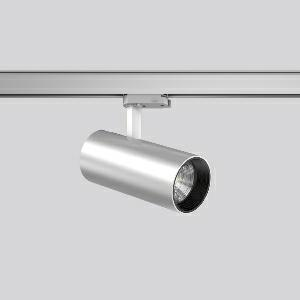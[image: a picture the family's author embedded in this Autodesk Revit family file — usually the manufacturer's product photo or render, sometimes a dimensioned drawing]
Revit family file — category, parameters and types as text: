
# Revit family: deecos_s_mini_742208_004_a754
name_source: partatom
category: Lighting Fixtures
units: mm (PartAtom-declared; Revit-internal decimal feet)

## family parameters
Cut with Voids When Loaded = No
Host = Face
Light Source = No
Part Type = Normal
Room Calculation Point = No
Round Connector Dimension = Use Diameter
Shared = No

## types (1)
- DEECOS S mini (1 x LED Modul 930, 2850 lm, 3000)
    Apparent Load = 29 VA
    Approval mark = CE
    CIE Flux Codes = 98 100 100 100 100
    Color Rendering = 90
    Color Temperature = 3000
    Default Elevation = 1800 mm
    Description = Series: DEECOS S mini
LED surface-mounted projector in modern design with no visible cooling ribs. Housing: die-cast aluminium, powder-coated. Rotation range: 356°. Swivel range: 90°. Black plastic ring and recessed LED to prevent glare from the side. Optical assembly with lens made of plastic (polycarbonate) for the best homogeneous light distribution - can be changed without tools. Best colour rendering index Ra>90. With multi adaptor for 3-circuit tracks 230 V. Suitable for Track on ceiling, Wall track. High quality converter without flickering and stroboscopic effect. The following accessories can be mounted without use of tools: interchangeable lenses, decorative glasses, honeycomb louvre, clear and frosted diffusers, white interchangeable plastic ring. 
Colour: silver
Diameter: 87 mm
Height: 214 mm
Lamp: LED
Socket: without socket
Colour temperature: 3000K
Colour rendering index (CRI): 92
System power: 29 W
Rated luminous flux: 2850 lm
Beam angle Down: 44°
Luminous efficiency: 98 lm/W
Control gear: Regulated power supply
Protection class: I
Type of protection: IP 20
    Height = 214 mm
    Lamp = 1 x LED Modul 930
    Lamp Light Flux = 2850 lm
    Lamp count = 1
    Length = 87 mm
    Lifetime = 50000 h
    Luminous efficacy = 98 lm/W
    Manufacturer = RZB
    ModVariant = No
    Model = 742208.004
    Mounting Place = Ceiling
    Mounting Type = Rail mounted
    Number of Poles = 1
    OnlyDefault = Yes
    Power Factor = 1
    Product Name = DEECOS S mini
    Product group = Track mounted projectors
    ProductGroupID = 301
    Protection Class = Protection class I
    Protection Degree = IP 20
    RLX_Detail_Level = 1
    RLX_Emergency_Light_Flux = 0 lm
    RLX_Emergency_Type = 0
    RLX_Emergency_Type_DB = No
    RlxData = <blob elided: 37601 chars, md5=7cfaf4fb>
    Socket = socket
    Standby Power = 0 W
    System Light Flux = 2850 lm
    System Power = 29 W
    Type Comments = ALEA SPOT
    Type Image = 741930.004.jpg
    URL = http://relux.com
    VarID = ---
    Voltage = 230 V
    Voltage Range = 220-240 V
    Weight = 0.00 kg
    Width = 0 mm  [stored 0 ft]

note: [stored X ft] marks values corroborated as IEEE doubles in the binary element streams (Revit-internal decimal feet)

## geometry (parser evidence)
native form markers: Blend x4, Sweep x11
no freeform markers — native parametric forms only
